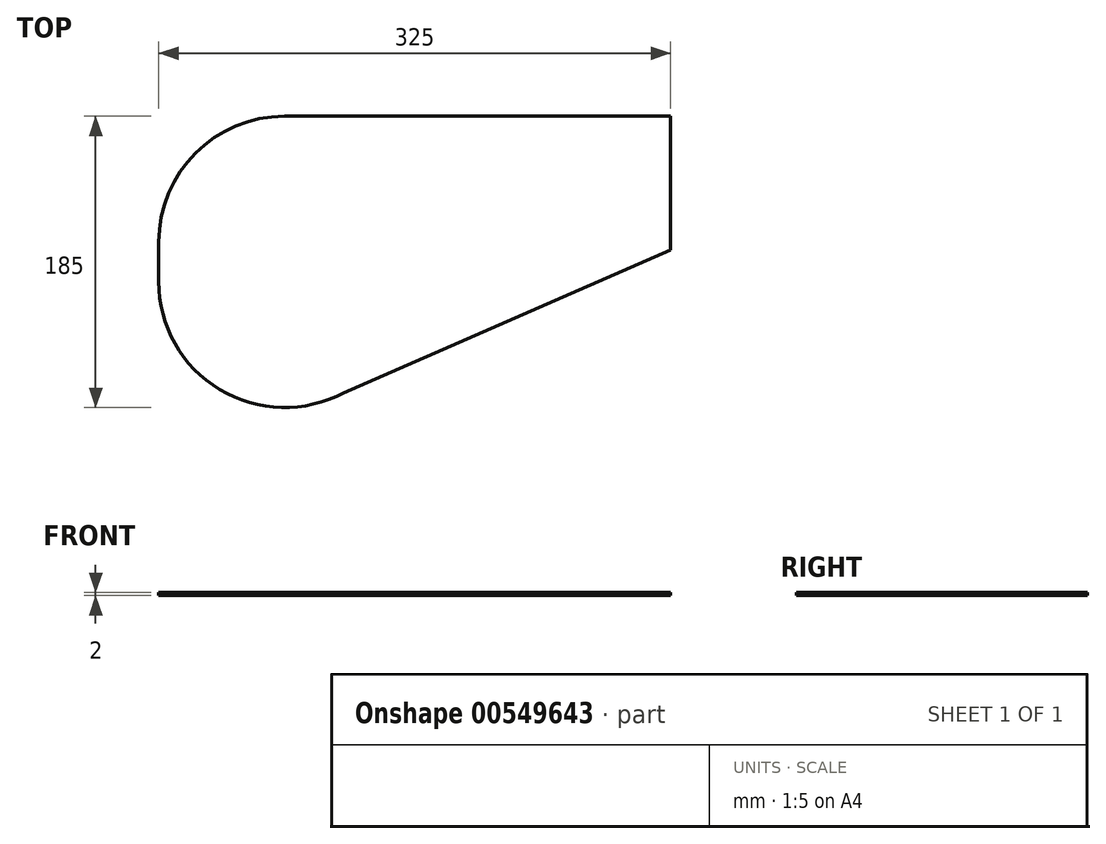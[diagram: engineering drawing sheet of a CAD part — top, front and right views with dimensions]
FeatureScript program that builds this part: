
annotation { "Feature Type Name" : "Feature", "Feature Type Description" : "" }
export const myFeature = defineFeature(function(context is Context, id is Id, definition is map)
    precondition{}
    {
        {
            var Q0;
            Q0=qCreatedBy(makeId("Top.planeOp"),FACE);
            var sketch = newSketch(context, id + "F0", { "sketchPlane" : qUnion([Q0])});
            skPoint(sketch, "E0.middle", {"position": v(0, 0) * mm});
            skPoint(sketch, "E1.MirrorP", {"position": v(-162.5, 0) * mm});
            skLineSegment(sketch, "E2.MirrorCS", {"start": v(-162.5, 12.5) * mm, "end": v(-162.5, -12.5) * mm});
            skLineSegment(sketch, "E3.MirrorCS", {"start": v(162.5, 92.5) * mm, "end": v(-82.5, 92.5) * mm});
            skLineSegment(sketch, "E4.MirrorCS", {"start": v(162.5, 7.5) * mm, "end": v(-44.96, -83.14) * mm});
            skArc(sketch, "E5.MirrorCS", {"start": v(-162.5, -12.5) * mm, "mid": v(-123.7, -81.07) * mm, "end": v(-44.96, -83.14) * mm});
            skLineSegment(sketch, "E6.MirrorCS", {"start": v(162.5, 92.5) * mm, "end": v(162.5, 7.5) * mm});
            skArc(sketch, "E7.MirrorCS", {"start": v(-82.5, 92.5) * mm, "mid": v(-139.07, 69.07) * mm, "end": v(-162.5, 12.5) * mm});
            skSolve(sketch);
        }
        {
            var Q0;
            Q0=makeQuery(id+"F0.imprint","IMPRINT",FACE,{"disambiguationData":[TD([[makeQuery(id+"F0.imprint","IMPRINT",EDGE,{"derivedFrom":sQuery(id+"F0.wireOp",EDGE,"E2.MirrorCS")}),1.0]])]});
            extrude(context, id + "F1", {"entities" : qUnion([Q0]), "depth" : 2 * mm, "offsetDistance" : 25 * mm});
        }
    });
